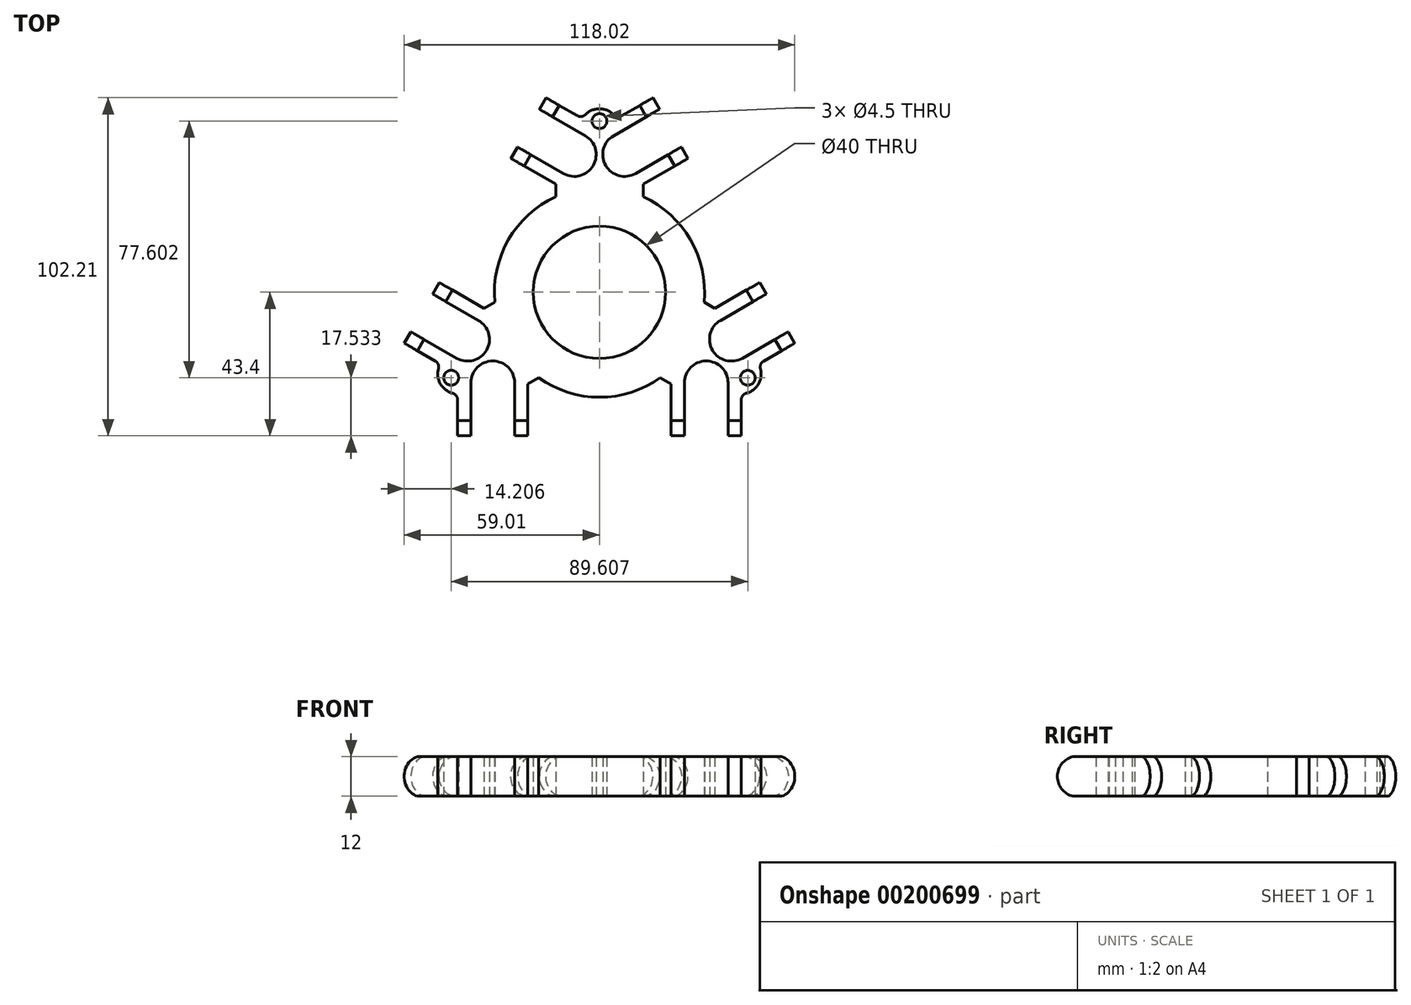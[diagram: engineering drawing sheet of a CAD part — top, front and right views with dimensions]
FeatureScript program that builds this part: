
annotation { "Feature Type Name" : "Feature", "Feature Type Description" : "" }
export const myFeature = defineFeature(function(context is Context, id is Id, definition is map)
    precondition{}
    {
        {
            var Q0;
            Q0=qCreatedBy(makeId("Top.planeOp"),FACE);
            var sketch = newSketch(context, id + "F0", { "sketchPlane" : qUnion([Q0])});
            skArc(sketch, "E0", {"start": v(-13.23, 28.86) * mm, "mid": v(-27.5, 15.87) * mm, "end": v(-31.61, -2.97) * mm});
            skLineSegment(sketch, "E1", {"start": v(0, 0) * mm, "end": v(51.65, 29.82) * mm, "construction": true});
            skLineSegment(sketch, "E2", {"start": v(0, 0) * mm, "end": v(-51.65, 29.82) * mm, "construction": true});
            skLineSegment(sketch, "E3", {"start": v(0, 0) * mm, "end": v(0, -59.64) * mm, "construction": true});
            skLineSegment(sketch, "E4", {"start": v(51.65, 29.82) * mm, "end": v(35.53, 57.75) * mm, "construction": true});
            skLineSegment(sketch, "E5.MirrorCS", {"start": v(51.65, 29.82) * mm, "end": v(67.78, 1.9) * mm, "construction": true});
            skLineSegment(sketch, "E6", {"start": v(35.53, 57.75) * mm, "end": v(7.6, 41.63) * mm, "construction": true});
            skArc(sketch, "E7", {"start": v(4.3, 47.34) * mm, "mid": v(1.88, 38.33) * mm, "end": v(10.9, 35.91) * mm});
            skLineSegment(sketch, "E8", {"start": v(4.3, 47.34) * mm, "end": v(18.16, 55.34) * mm});
            skLineSegment(sketch, "E9.MirrorCS", {"start": v(10.9, 35.91) * mm, "end": v(24.76, 43.91) * mm});
            skLineSegment(sketch, "E10", {"start": v(24.76, 43.91) * mm, "end": v(26.76, 40.45) * mm});
            skLineSegment(sketch, "E11", {"start": v(26.76, 40.45) * mm, "end": v(13.23, 32.64) * mm});
            skLineSegment(sketch, "E12", {"start": v(18.16, 55.34) * mm, "end": v(16.16, 58.8) * mm});
            skLineSegment(sketch, "E13", {"start": v(16.16, 58.8) * mm, "end": v(6.7, 53.35) * mm});
            skArc(sketch, "E14", {"start": v(4.28, 53.68) * mm, "mid": v(0, 55.48) * mm, "end": v(-4.28, 53.68) * mm});
            skLineSegment(sketch, "E15.MirrorCS", {"start": v(-26.76, 40.45) * mm, "end": v(-13.23, 32.64) * mm});
            skLineSegment(sketch, "E16.MirrorCS", {"start": v(-24.76, 43.91) * mm, "end": v(-26.76, 40.45) * mm});
            skLineSegment(sketch, "E17.MirrorCS", {"start": v(-10.9, 35.91) * mm, "end": v(-24.76, 43.91) * mm});
            skArc(sketch, "E18.MirrorCS", {"start": v(-4.3, 47.34) * mm, "mid": v(-1.88, 38.33) * mm, "end": v(-10.9, 35.91) * mm});
            skLineSegment(sketch, "E19.MirrorCS", {"start": v(-4.3, 47.34) * mm, "end": v(-18.16, 55.34) * mm});
            skLineSegment(sketch, "E20.MirrorCS", {"start": v(-18.16, 55.34) * mm, "end": v(-16.16, 58.8) * mm});
            skLineSegment(sketch, "E21.MirrorCS", {"start": v(-16.16, 58.8) * mm, "end": v(-6.7, 53.35) * mm});
            skCircle(sketch, "E22", {"center": v(0, 51.73) * mm, "radius": 2.25 * mm});
            skPoint(sketch, "E22.centerSnap0", {"position": v(0, 55.48) * mm});
            skPoint(sketch, "E23.visualSharp", {"position": v(-5.2, 52.48) * mm});
            skArc(sketch, "E23.filletArc", {"start": v(-6.7, 53.35) * mm, "mid": v(-5.44, 53.1) * mm, "end": v(-4.28, 53.68) * mm});
            skPoint(sketch, "E24.visualSharp", {"position": v(5.2, 52.48) * mm});
            skArc(sketch, "E24.filletArc", {"start": v(4.28, 53.68) * mm, "mid": v(5.44, 53.1) * mm, "end": v(6.7, 53.35) * mm});
            skLineSegment(sketch, "E25", {"start": v(13.23, 32.64) * mm, "end": v(13.23, 28.86) * mm});
            skLineSegment(sketch, "E26.MirrorCS", {"start": v(-13.23, 32.64) * mm, "end": v(-13.23, 28.86) * mm});
            skPoint(sketch, "E27.1.0", {"position": v(48.05, -21.74) * mm});
            skLineSegment(sketch, "E27.1.1", {"start": v(59, -15.41) * mm, "end": v(49.56, -20.87) * mm});
            skArc(sketch, "E27.1.2", {"start": v(43.15, -19.95) * mm, "mid": v(34.13, -17.53) * mm, "end": v(36.55, -8.52) * mm});
            skLineSegment(sketch, "E27.1.3", {"start": v(38.85, -27.4) * mm, "end": v(38.85, -43.4) * mm});
            skLineSegment(sketch, "E27.1.4", {"start": v(21.65, -43.4) * mm, "end": v(21.65, -27.78) * mm});
            skCircle(sketch, "E27.1.5", {"center": v(44.8, -25.87) * mm, "radius": 2.25 * mm});
            skArc(sketch, "E27.1.6", {"start": v(38.85, -27.4) * mm, "mid": v(32.25, -20.8) * mm, "end": v(25.65, -27.4) * mm});
            skLineSegment(sketch, "E27.1.7", {"start": v(25.65, -27.4) * mm, "end": v(25.65, -43.4) * mm});
            skPoint(sketch, "E27.1.8", {"position": v(48.05, -27.74) * mm});
            skLineSegment(sketch, "E27.1.9", {"start": v(36.55, -8.52) * mm, "end": v(50.4, -0.52) * mm});
            skLineSegment(sketch, "E27.1.10", {"start": v(48.4, 2.95) * mm, "end": v(34.88, -4.86) * mm});
            skLineSegment(sketch, "E27.1.11", {"start": v(42.85, -43.4) * mm, "end": v(42.85, -32.49) * mm});
            skPoint(sketch, "E27.1.12", {"position": v(42.85, -30.74) * mm});
            skLineSegment(sketch, "E27.1.13", {"start": v(43.15, -19.95) * mm, "end": v(57, -11.95) * mm});
            skArc(sketch, "E27.1.14", {"start": v(44.35, -30.55) * mm, "mid": v(48.05, -27.74) * mm, "end": v(48.63, -23.13) * mm});
            skLineSegment(sketch, "E27.1.15", {"start": v(21.65, -27.78) * mm, "end": v(18.38, -25.9) * mm});
            skLineSegment(sketch, "E27.1.16", {"start": v(48.4, 2.95) * mm, "end": v(34.88, -4.86) * mm});
            skLineSegment(sketch, "E27.1.17", {"start": v(34.88, -4.86) * mm, "end": v(31.61, -2.97) * mm});
            skArc(sketch, "E27.1.18", {"start": v(49.56, -20.87) * mm, "mid": v(48.7, -21.84) * mm, "end": v(48.63, -23.13) * mm});
            skLineSegment(sketch, "E27.1.19", {"start": v(38.85, -43.4) * mm, "end": v(42.85, -43.4) * mm});
            skLineSegment(sketch, "E27.1.20", {"start": v(50.4, -0.52) * mm, "end": v(48.4, 2.95) * mm});
            skArc(sketch, "E27.1.21", {"start": v(44.35, -30.55) * mm, "mid": v(43.27, -31.26) * mm, "end": v(42.85, -32.49) * mm});
            skLineSegment(sketch, "E27.1.22", {"start": v(25.65, -43.4) * mm, "end": v(21.65, -43.4) * mm});
            skLineSegment(sketch, "E27.1.23", {"start": v(57, -11.95) * mm, "end": v(59, -15.41) * mm});
            skPoint(sketch, "E27.2.0", {"position": v(-42.85, -30.74) * mm});
            skLineSegment(sketch, "E27.2.1", {"start": v(-42.85, -43.4) * mm, "end": v(-42.85, -32.49) * mm});
            skArc(sketch, "E27.2.2", {"start": v(-38.85, -27.4) * mm, "mid": v(-32.25, -20.8) * mm, "end": v(-25.65, -27.4) * mm});
            skLineSegment(sketch, "E27.2.3", {"start": v(-43.15, -19.95) * mm, "end": v(-57, -11.95) * mm});
            skLineSegment(sketch, "E27.2.4", {"start": v(-48.4, 2.95) * mm, "end": v(-34.88, -4.86) * mm});
            skCircle(sketch, "E27.2.5", {"center": v(-44.8, -25.87) * mm, "radius": 2.25 * mm});
            skArc(sketch, "E27.2.6", {"start": v(-43.15, -19.95) * mm, "mid": v(-34.13, -17.53) * mm, "end": v(-36.55, -8.52) * mm});
            skLineSegment(sketch, "E27.2.7", {"start": v(-36.55, -8.52) * mm, "end": v(-50.4, -0.52) * mm});
            skPoint(sketch, "E27.2.8", {"position": v(-48.05, -27.74) * mm});
            skLineSegment(sketch, "E27.2.9", {"start": v(-25.65, -27.4) * mm, "end": v(-25.65, -43.4) * mm});
            skLineSegment(sketch, "E27.2.10", {"start": v(-21.65, -43.4) * mm, "end": v(-21.65, -27.78) * mm});
            skLineSegment(sketch, "E27.2.11", {"start": v(-59, -15.41) * mm, "end": v(-49.56, -20.87) * mm});
            skPoint(sketch, "E27.2.12", {"position": v(-48.05, -21.74) * mm});
            skLineSegment(sketch, "E27.2.13", {"start": v(-38.85, -27.4) * mm, "end": v(-38.85, -43.4) * mm});
            skArc(sketch, "E27.2.14", {"start": v(-48.63, -23.13) * mm, "mid": v(-48.05, -27.74) * mm, "end": v(-44.35, -30.55) * mm});
            skLineSegment(sketch, "E27.2.15", {"start": v(-34.88, -4.86) * mm, "end": v(-31.61, -2.97) * mm});
            skLineSegment(sketch, "E27.2.16", {"start": v(-21.65, -43.4) * mm, "end": v(-21.65, -27.78) * mm});
            skLineSegment(sketch, "E27.2.17", {"start": v(-21.65, -27.78) * mm, "end": v(-18.38, -25.9) * mm});
            skArc(sketch, "E27.2.18", {"start": v(-42.85, -32.49) * mm, "mid": v(-43.27, -31.26) * mm, "end": v(-44.35, -30.55) * mm});
            skLineSegment(sketch, "E27.2.19", {"start": v(-57, -11.95) * mm, "end": v(-59, -15.41) * mm});
            skLineSegment(sketch, "E27.2.20", {"start": v(-25.65, -43.4) * mm, "end": v(-21.65, -43.4) * mm});
            skArc(sketch, "E27.2.21", {"start": v(-48.63, -23.13) * mm, "mid": v(-48.7, -21.84) * mm, "end": v(-49.56, -20.87) * mm});
            skLineSegment(sketch, "E27.2.22", {"start": v(-50.4, -0.52) * mm, "end": v(-48.4, 2.95) * mm});
            skLineSegment(sketch, "E27.2.23", {"start": v(-38.85, -43.4) * mm, "end": v(-42.85, -43.4) * mm});
            skLineSegment(sketch, "E27.anchor1", {"start": v(0, 0) * mm, "end": v(0, 55.48) * mm, "construction": true});
            skArc(sketch, "E28.trimOffspring", {"start": v(-18.38, -25.9) * mm, "mid": v(0, -31.75) * mm, "end": v(18.38, -25.9) * mm});
            skArc(sketch, "E29.trimOffspring", {"start": v(31.61, -2.97) * mm, "mid": v(27.5, 15.88) * mm, "end": v(13.23, 28.86) * mm});
            skCircle(sketch, "E30", {"center": v(0, 0) * mm, "radius": 20 * mm});
            skSolve(sketch);
        }
        {
            var Q0;
            Q0=makeQuery(id+"F0.imprint","IMPRINT",FACE,{"disambiguationData":[TD([[makeQuery(id+"F0.imprint","IMPRINT",EDGE,{"derivedFrom":sQuery(id+"F0.wireOp",EDGE,"E0")}),1.0]])]});
            extrude(context, id + "F1", {"entities" : qUnion([Q0]), "depth" : 12 * mm});
        }
        {
            var Q0;
            Q0=makeQuery(id+"F1.opExtrude","SWEPT_FACE",FACE,{"disambiguationData":[OSD([sQuery(id+"F0.wireOp",EDGE,"E27.1.4")])]});
            var sketch = newSketch(context, id + "F2", { "sketchPlane" : qUnion([Q0])});
            skArc(sketch, "E31", {"start": v(37.21, -0.2) * mm, "mid": v(43.4, 6) * mm, "end": v(37.21, 12.2) * mm});
            skPoint(sketch, "E31.second.point", {"position": v(43.4, 6) * mm});
            skLineSegment(sketch, "E32", {"start": v(37.21, -0.2) * mm, "end": v(37.21, -2.75) * mm});
            skLineSegment(sketch, "E33", {"start": v(37.21, -2.75) * mm, "end": v(50.04, -2.75) * mm});
            skLineSegment(sketch, "E34", {"start": v(50.04, -2.75) * mm, "end": v(50.04, 14.75) * mm});
            skLineSegment(sketch, "E35", {"start": v(50.04, 14.75) * mm, "end": v(37.21, 14.75) * mm});
            skLineSegment(sketch, "E36", {"start": v(37.21, 12.2) * mm, "end": v(37.21, 14.75) * mm});
            skSolve(sketch);
        }
        {
            var Q0;
            Q0=makeQuery(id+"F1.opExtrude","SWEPT_FACE",FACE,{"disambiguationData":[OSD([sQuery(id+"F0.wireOp",EDGE,"E11")])]});
            var sketch = newSketch(context, id + "F3", { "sketchPlane" : qUnion([Q0])});
            skArc(sketch, "E37", {"start": v(37.21, -0.2) * mm, "mid": v(43.4, 6) * mm, "end": v(37.21, 12.2) * mm});
            skPoint(sketch, "E37.second.point", {"position": v(43.4, 6) * mm});
            skLineSegment(sketch, "E38", {"start": v(37.21, -0.2) * mm, "end": v(37.21, -2.75) * mm});
            skLineSegment(sketch, "E39", {"start": v(37.21, -2.75) * mm, "end": v(50.04, -2.75) * mm});
            skLineSegment(sketch, "E40", {"start": v(50.04, -2.75) * mm, "end": v(50.04, 14.75) * mm});
            skLineSegment(sketch, "E41", {"start": v(50.04, 14.75) * mm, "end": v(37.21, 14.75) * mm});
            skLineSegment(sketch, "E42", {"start": v(37.21, 12.2) * mm, "end": v(37.21, 14.75) * mm});
            skSolve(sketch);
        }
        {
            var Q0;
            Q0=makeQuery(id+"F1.opExtrude","SWEPT_FACE",FACE,{"disambiguationData":[OSD([sQuery(id+"F0.wireOp",EDGE,"E27.2.4")])]});
            var sketch = newSketch(context, id + "F4", { "sketchPlane" : qUnion([Q0])});
            skArc(sketch, "E43", {"start": v(37.21, -0.2) * mm, "mid": v(43.4, 6) * mm, "end": v(37.21, 12.2) * mm});
            skPoint(sketch, "E43.second.point", {"position": v(43.4, 6) * mm});
            skLineSegment(sketch, "E44", {"start": v(37.21, -0.2) * mm, "end": v(37.21, -2.75) * mm});
            skLineSegment(sketch, "E45", {"start": v(37.21, -2.75) * mm, "end": v(50.04, -2.75) * mm});
            skLineSegment(sketch, "E46", {"start": v(50.04, -2.75) * mm, "end": v(50.04, 14.75) * mm});
            skLineSegment(sketch, "E47", {"start": v(50.04, 14.75) * mm, "end": v(37.21, 14.75) * mm});
            skLineSegment(sketch, "E48", {"start": v(37.21, 12.2) * mm, "end": v(37.21, 14.75) * mm});
            skSolve(sketch);
        }
        {
            var Q0;
            {var subQ0=sQuery(id+"F2.wireOp",EDGE,"E31");var subQ1=sQuery(id+"F0.wireOp",EDGE,"E27.1.4");var subQ2=makeQuery(id+"F1.opExtrude","CAP_EDGE",EDGE,{"disambiguationData":[OSD([subQ1])],"isStart":false});var subQ3=makeQuery(id+"F2.imprint","INTERSECT",VERTEX,{"derivedFrom":[subQ2,subQ0]});Q0=makeQuery(id+"F2.imprint","IMPRINT",FACE,{"disambiguationData":[TD([[makeQuery(id+"F2.imprint","IMPRINT",EDGE,{"disambiguationData":[TD([[subQ3,1.0]])],"derivedFrom":subQ0}),-1.0]])]});}
            var Q1;
            {var subQ6=sQuery(id+"F2.wireOp",EDGE,"E32");Q1=makeQuery(id+"F2.imprint","IMPRINT",FACE,{"disambiguationData":[TD([[makeQuery(id+"F2.imprint","IMPRINT",EDGE,{"derivedFrom":subQ6}),1.0]])]});}
            var Q2;
            {var subQ0=sQuery(id+"F2.wireOp",EDGE,"E31");var subQ1=sQuery(id+"F0.wireOp",EDGE,"E27.1.4");var subQ2=makeQuery(id+"F1.opExtrude","CAP_EDGE",EDGE,{"disambiguationData":[OSD([subQ1])],"isStart":true});var subQ3=makeQuery(id+"F2.imprint","INTERSECT",VERTEX,{"derivedFrom":[subQ2,subQ0]});Q2=makeQuery(id+"F2.imprint","IMPRINT",FACE,{"disambiguationData":[TD([[makeQuery(id+"F2.imprint","IMPRINT",EDGE,{"disambiguationData":[TD([[subQ3,-1.0]])],"derivedFrom":subQ0}),-1.0]])]});}
            extrude(context, id + "F5", {"entities" : qUnion([Q0, Q1, Q2]), "operationType" : NewBodyOperationType.REMOVE, "oppositeDirection" : true, "depth" : 25 * mm, "hasSecondDirection" : true, "secondDirectionOppositeDirection" : false, "secondDirectionDepth" : 68 * mm});
        }
        {
            var Q0;
            {var subQ11=sQuery(id+"F3.wireOp",EDGE,"E38");Q0=makeQuery(id+"F3.imprint","IMPRINT",FACE,{"disambiguationData":[TD([[makeQuery(id+"F3.imprint","IMPRINT",EDGE,{"derivedFrom":subQ11}),1.0]])]});}
            var Q1;
            {var subQ0=sQuery(id+"F3.wireOp",EDGE,"E37");var subQ1=sQuery(id+"F0.wireOp",EDGE,"E11");var subQ2=makeQuery(id+"F1.opExtrude","CAP_EDGE",EDGE,{"disambiguationData":[OSD([subQ1])],"isStart":false});var subQ3=makeQuery(id+"F3.imprint","INTERSECT",VERTEX,{"derivedFrom":[subQ2,subQ0]});Q1=makeQuery(id+"F3.imprint","IMPRINT",FACE,{"disambiguationData":[TD([[makeQuery(id+"F3.imprint","IMPRINT",EDGE,{"disambiguationData":[TD([[subQ3,1.0]])],"derivedFrom":subQ0}),-1.0]])]});}
            var Q2;
            {var subQ0=sQuery(id+"F3.wireOp",EDGE,"E37");var subQ1=sQuery(id+"F0.wireOp",EDGE,"E11");var subQ2=makeQuery(id+"F1.opExtrude","CAP_EDGE",EDGE,{"disambiguationData":[OSD([subQ1])],"isStart":true});var subQ3=makeQuery(id+"F3.imprint","INTERSECT",VERTEX,{"derivedFrom":[subQ2,subQ0]});Q2=makeQuery(id+"F3.imprint","IMPRINT",FACE,{"disambiguationData":[TD([[makeQuery(id+"F3.imprint","IMPRINT",EDGE,{"disambiguationData":[TD([[subQ3,-1.0]])],"derivedFrom":subQ0}),-1.0]])]});}
            extrude(context, id + "F6", {"entities" : qUnion([Q0, Q1, Q2]), "operationType" : NewBodyOperationType.REMOVE, "oppositeDirection" : true, "depth" : 25 * mm, "hasSecondDirection" : true, "secondDirectionOppositeDirection" : false, "secondDirectionDepth" : 68 * mm});
        }
        {
            var Q0;
            {var subQ10=sQuery(id+"F4.wireOp",EDGE,"E44");Q0=makeQuery(id+"F4.imprint","IMPRINT",FACE,{"disambiguationData":[TD([[makeQuery(id+"F4.imprint","IMPRINT",EDGE,{"derivedFrom":subQ10}),1.0]])]});}
            var Q1;
            {var subQ0=sQuery(id+"F4.wireOp",EDGE,"E43");var subQ1=sQuery(id+"F0.wireOp",EDGE,"E27.2.4");var subQ2=makeQuery(id+"F1.opExtrude","CAP_EDGE",EDGE,{"disambiguationData":[OSD([subQ1])],"isStart":true});var subQ3=makeQuery(id+"F4.imprint","INTERSECT",VERTEX,{"derivedFrom":[subQ2,subQ0]});Q1=makeQuery(id+"F4.imprint","IMPRINT",FACE,{"disambiguationData":[TD([[makeQuery(id+"F4.imprint","IMPRINT",EDGE,{"disambiguationData":[TD([[subQ3,-1.0]])],"derivedFrom":subQ0}),-1.0]])]});}
            var Q2;
            {var subQ0=sQuery(id+"F4.wireOp",EDGE,"E43");var subQ1=sQuery(id+"F0.wireOp",EDGE,"E27.2.4");var subQ2=makeQuery(id+"F1.opExtrude","CAP_EDGE",EDGE,{"disambiguationData":[OSD([subQ1])],"isStart":false});var subQ3=makeQuery(id+"F4.imprint","INTERSECT",VERTEX,{"derivedFrom":[subQ2,subQ0]});Q2=makeQuery(id+"F4.imprint","IMPRINT",FACE,{"disambiguationData":[TD([[makeQuery(id+"F4.imprint","IMPRINT",EDGE,{"disambiguationData":[TD([[subQ3,1.0]])],"derivedFrom":subQ0}),-1.0]])]});}
            extrude(context, id + "F7", {"entities" : qUnion([Q0, Q1, Q2]), "operationType" : NewBodyOperationType.REMOVE, "oppositeDirection" : true, "depth" : 25 * mm, "hasSecondDirection" : true, "secondDirectionOppositeDirection" : false, "secondDirectionDepth" : 68 * mm});
        }
    });
